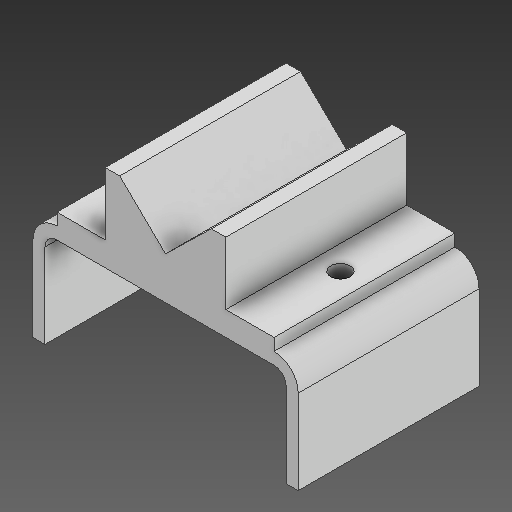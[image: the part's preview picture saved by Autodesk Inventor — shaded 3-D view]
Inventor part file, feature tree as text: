
AUTODESK INVENTOR PART (.ipt)
format: ipt  version: 2021 (Build 250183000, 183)  size: 143,872 bytes
history: native  units: in
note: dims shown in document units (in); Inventor stores cm internally (conversion verified against a paired STEP export)
features: other x3, sketch x2
ambient origin geometry x8: Origin, YZ Plane, XZ Plane, XY Plane, X Axis, Y Axis, Z Axis, Center Point
bodies: Solid1 (feature_tree)
feature tree (5):
  other  "Base soporte tubos.ipt"
  other  "Solid1::Base soporte tubos.ipt"
  other  "TaggingFeature1"
  sketch  "Sketch1"  dims[d0=0.3937in]
  sketch  "Sketch4"
